# Revit family: Gewindestange
name_source: partatom
category: HLS-Bauteile
units: mm (PartAtom-declared; Revit-internal decimal feet)

## family parameters
Arbeitsebenenbasiert = Ja
Beim Laden mit Abzugskörper schneiden = Nein
Bemaßung runder Anschluss = Durchmesser verwenden
Beschriftungsausrichtung beibehalten = Nein
Gemeinsam genutzt = Ja
Immer vertikal = Nein
Raumberechnungspunkt = Nein
Teiletyp = Normal

## types (12) — shared parameters
Fabrikat = MEFA
Festigkeitsklasse = 4.6
Kurztext1 = Gewindestange DIN 976-1
Material = Stahl
Mengeneinheit = St
Vorgabe-Ansicht = 1219 mm

## per-type parameters (varying)
| type | Artikelnummer | Bund | D | EAN | Gewicht | Gewinde | Kurztext2 | Länge | vpe |
| Gewindestange M8x1000 | 0730084 | 50 St | 7 mm  [stored 0.0229659 ft] | 4250928416452 | 0.33 kg | M8 | M8 x 1.000 mm gvz FK 4.6 | 1000 mm  [stored 3.28084 ft] | 50 |
| Gewindestange M8x2000 | 0730289 | 25 St | 7 mm  [stored 0.0229659 ft] | 4250928416490 | 0.65 kg | M8 | M8 x 2.000 mm gvz FK 4.6 | 2000 mm  [stored 6.56168 ft] | 25 |
| Gewindestange M8x3000 | 0730483 | 50 St | 7 mm  [stored 0.0229659 ft] | 4250928416537 | 0.98 kg | M8 | M8 x 3.000 mm gvz FK 4.6 | 3000 mm  [stored 9.84252 ft] | 50 |
| Gewindestange M10x1000 | 0730106 | 25 St | 8 mm  [stored 0.0262467 ft] | 4250928416469 | 0.51 kg | M10 | M10 x 1.000 mm gvz FK 4.6 | 1000 mm  [stored 3.28084 ft] | 25 |
| Gewindestange M10x2000 | 0730300 | 20 St | 8 mm  [stored 0.0262467 ft] | 4250928416506 | 1.02 kg | M10 | M10 x 2.000 mm gvz FK 4.6 | 2000 mm  [stored 6.56168 ft] | 20 |
| Gewindestange M10x3000 | 0730505 | 25 St | 8 mm  [stored 0.0262467 ft] | 4250928416544 | 1.53 kg | M10 | M10 x 3.000 mm gvz FK 4.6 | 3000 mm  [stored 9.84252 ft] | 25 |
| Gewindestange M12x1000 | 0730122 | 25 St | 10 mm  [stored 0.0328084 ft] | 4250928416476 | 0.74 kg | M12 | M12 x 1.000 mm gvz FK 4.6 | 1000 mm  [stored 3.28084 ft] | 25 |
| Gewindestange M12x2000 | 0730327 | 20 St | 10 mm  [stored 0.0328084 ft] | 4250928416513 | 1.47 kg | M12 | M12 x 2.000 mm gvz FK 4.6 | 2000 mm  [stored 6.56168 ft] | 20 |
| Gewindestange M12x3000 | 0730521 | 25 St | 10 mm  [stored 0.0328084 ft] | 4250928416551 | 2.21 kg | M12 | M12 x 3.000 mm gvz FK 4.6 | 3000 mm  [stored 9.84252 ft] | 25 |
| Gewindestange M16x1000 | 0730165 | 10 St | 14 mm  [stored 0.0459318 ft] | 4250928416483 | 1.31 kg | M16 | M16 x 1.000 mm gvz FK 4.6 | 1000 mm  [stored 3.28084 ft] | 10 |
| Gewindestange M16x2000 | 0730378 | 10 St | 14 mm  [stored 0.0459318 ft] | 4250928416520 | 2.61 kg | M16 | M16 x 2.000 mm gvz FK 4.6 | 2000 mm  [stored 6.56168 ft] | 10 |
| Gewindestange M16x3000 | 0730564 | 20 St | 14 mm  [stored 0.0459318 ft] | 4250928416568 | 3.92 kg | M16 | M16 x 3.000 mm gvz FK 4.6 | 3000 mm  [stored 9.84252 ft] | 20 |

note: [stored X ft] marks values corroborated as IEEE doubles in the binary element streams (Revit-internal decimal feet)
